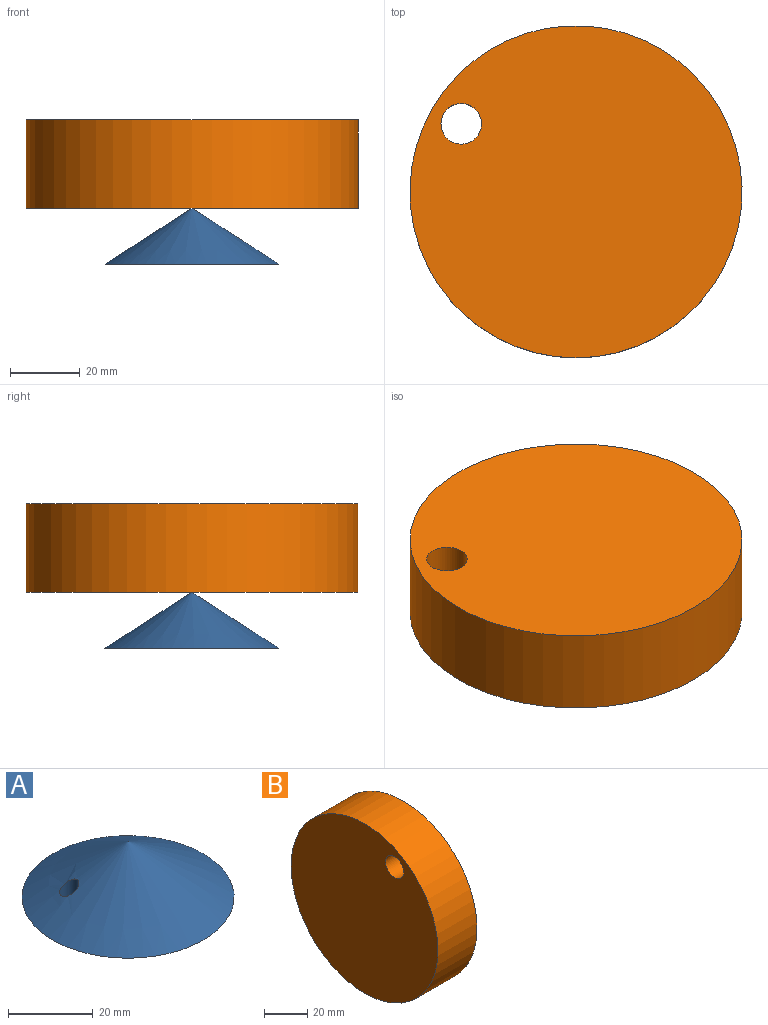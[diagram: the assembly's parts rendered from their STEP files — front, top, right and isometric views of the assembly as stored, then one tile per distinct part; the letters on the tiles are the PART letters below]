
ASSEMBLY  parts=2 mates=1
PART A: 3 faces, bbox 50x50x16.1 mm
  f0: cone r=25mm half-angle=57.3deg, axis (0,0,-1), area 2314.1mm2, adj f1,f2
  f1: plane 50x50mm, normal (0,0,-1), area 1947.2mm2, adj f0,f2
  f2: cylinder r=2.27mm len=7.97mm, axis (0,0,-1), area 92.1mm2, adj f0,f1
PART B: 4 faces, bbox 25.4x95.6x95.6 mm
  f0: cylinder r=5.84mm len=25.4mm, axis (-1,0,0), area 932.4mm2, adj f2,f3
  f1: cylinder r=47.78mm len=95.56mm, axis (-1,0,0), area 7625.3mm2, adj f2,f3
  f2: plane 95.56x95.56mm, normal (1,0,0), area 7064.7mm2, adj f0,f1
  f3: plane 95.56x95.56mm, normal (-1,0,0), area 7064.7mm2, adj f0,f1
PLACE A rot(axis=(0,0,-1),150.7deg) t=(0,0,0)mm
PLACE B rot(axis=(0.71,0,-0.71),180deg) t=(-121.72,-79.34,41.45)mm fixed
MATE revolute B.f1 <-> A.f0  axis (0,0,-1) through (0,0,16.05)mm
